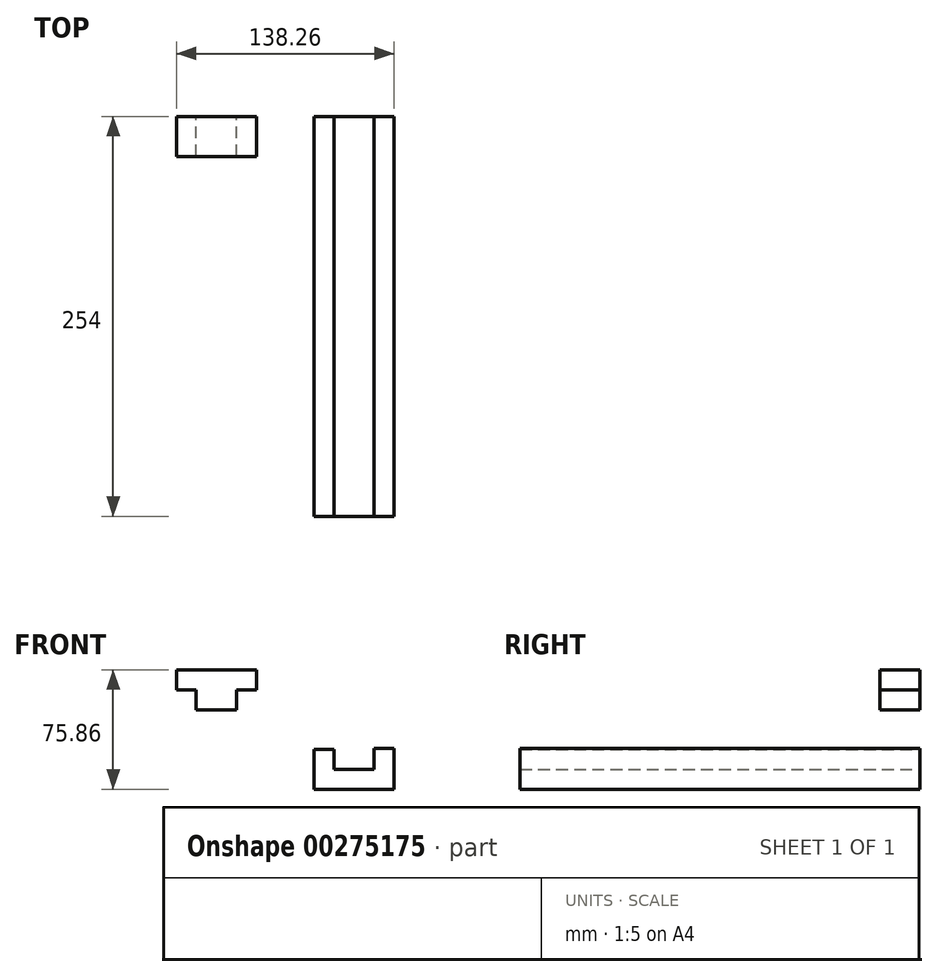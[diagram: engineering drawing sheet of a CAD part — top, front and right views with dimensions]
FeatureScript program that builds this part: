
annotation { "Feature Type Name" : "Feature", "Feature Type Description" : "" }
export const myFeature = defineFeature(function(context is Context, id is Id, definition is map)
    precondition{}
    {
        {
            var Q0;
            Q0=qCreatedBy(makeId("Front.planeOp"),FACE);
            var sketch = newSketch(context, id + "F0", { "sketchPlane" : qUnion([Q0])});
            skLineSegment(sketch, "E0", {"start": v(0, 0) * mm, "end": v(0, 25.4) * mm});
            skLineSegment(sketch, "E1", {"start": v(0, 25.4) * mm, "end": v(12.7, 25.4) * mm});
            skLineSegment(sketch, "E2", {"start": v(12.7, 25.4) * mm, "end": v(12.7, 12.7) * mm});
            skLineSegment(sketch, "E3", {"start": v(12.7, 12.7) * mm, "end": v(38.1, 12.7) * mm});
            skLineSegment(sketch, "E4", {"start": v(38.1, 12.7) * mm, "end": v(38.1, 25.73) * mm});
            skLineSegment(sketch, "E5", {"start": v(38.1, 25.73) * mm, "end": v(50.8, 25.73) * mm});
            skLineSegment(sketch, "E6", {"start": v(50.8, 25.73) * mm, "end": v(50.8, 0) * mm});
            skLineSegment(sketch, "E7", {"start": v(50.8, 0) * mm, "end": v(0, 0) * mm});
            skSolve(sketch);
        }
        {
            var Q0;
            Q0=makeQuery(id+"F0.imprint","IMPRINT",FACE,{"disambiguationData":[TD([[makeQuery(id+"F0.imprint","IMPRINT",EDGE,{"derivedFrom":sQuery(id+"F0.wireOp",EDGE,"E0")}),-1.0]])]});
            extrude(context, id + "F1", {"entities" : qUnion([Q0]), "depth" : 254 * mm});
        }
        {
            var Q0;
            Q0=qCreatedBy(makeId("Front.planeOp"),FACE);
            var sketch = newSketch(context, id + "F2", { "sketchPlane" : qUnion([Q0])});
            skLineSegment(sketch, "E8", {"start": v(-74.76, 63.16) * mm, "end": v(-74.76, 50.46) * mm});
            skLineSegment(sketch, "E9", {"start": v(-74.76, 50.46) * mm, "end": v(-49.36, 50.46) * mm});
            skLineSegment(sketch, "E10", {"start": v(-49.36, 50.46) * mm, "end": v(-49.36, 63.16) * mm});
            skLineSegment(sketch, "E11", {"start": v(-49.36, 63.16) * mm, "end": v(-36.66, 63.16) * mm});
            skLineSegment(sketch, "E12", {"start": v(-36.66, 63.16) * mm, "end": v(-36.66, 75.86) * mm});
            skLineSegment(sketch, "E13", {"start": v(-36.66, 75.86) * mm, "end": v(-87.46, 75.86) * mm});
            skLineSegment(sketch, "E14", {"start": v(-87.46, 75.86) * mm, "end": v(-87.46, 63.16) * mm});
            skLineSegment(sketch, "E15", {"start": v(-87.46, 63.16) * mm, "end": v(-74.76, 63.16) * mm});
            skSolve(sketch);
        }
        {
            var Q0;
            Q0=makeQuery(id+"F2.imprint","IMPRINT",FACE,{"disambiguationData":[TD([[makeQuery(id+"F2.imprint","IMPRINT",EDGE,{"derivedFrom":sQuery(id+"F2.wireOp",EDGE,"E8")}),1.0]])]});
            extrude(context, id + "F3", {"entities" : qUnion([Q0]), "depth" : 25.4 * mm});
        }
    });
